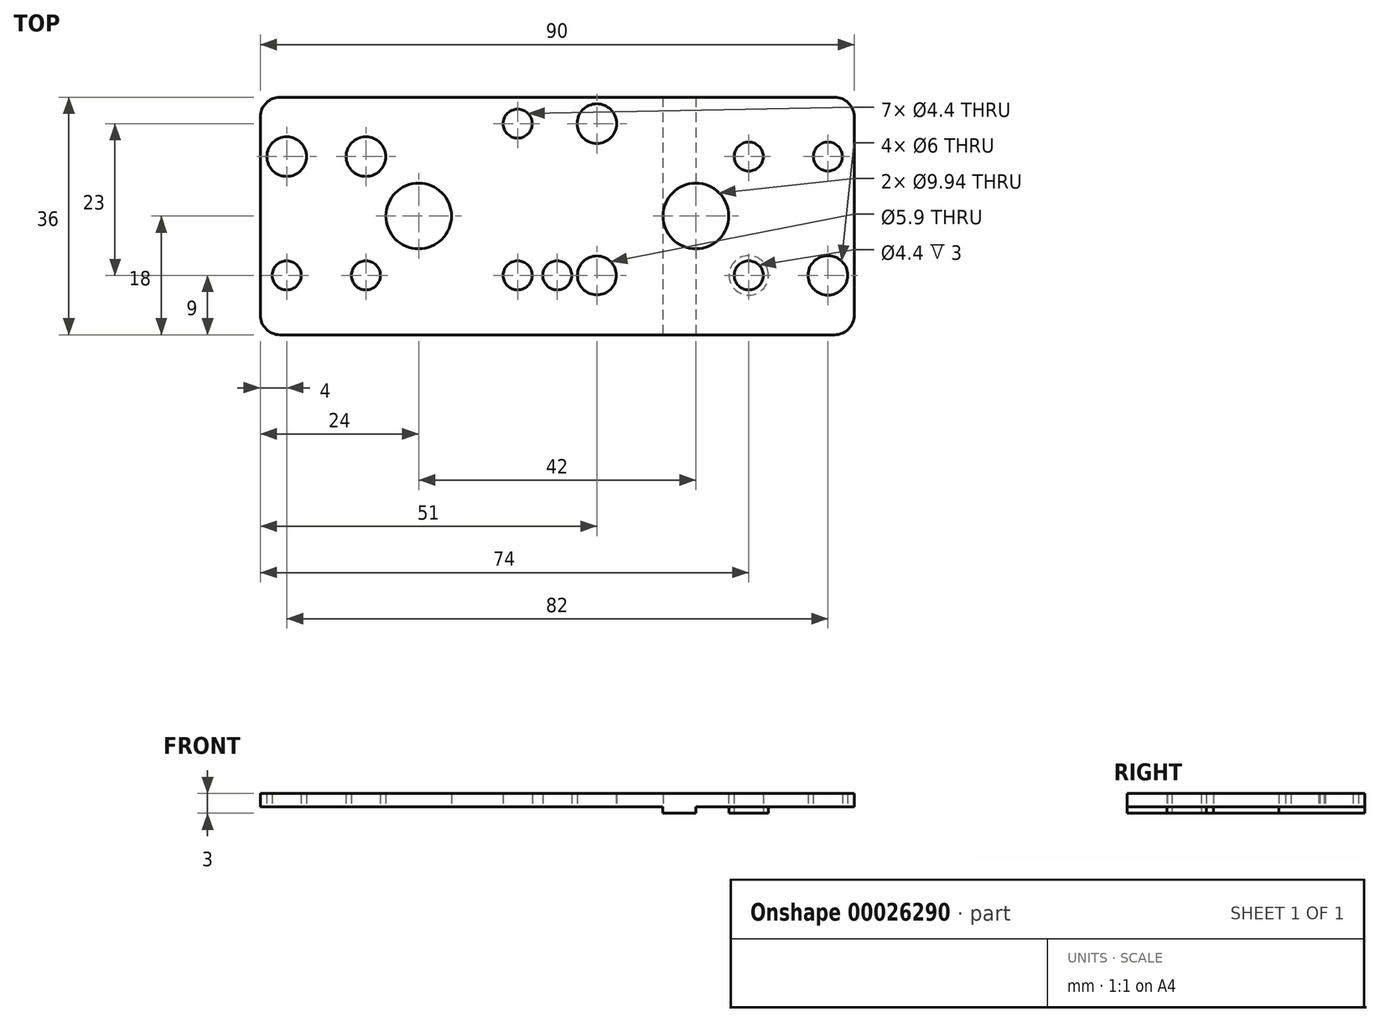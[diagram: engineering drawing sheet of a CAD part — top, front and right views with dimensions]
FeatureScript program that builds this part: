
annotation { "Feature Type Name" : "Feature", "Feature Type Description" : "" }
export const myFeature = defineFeature(function(context is Context, id is Id, definition is map)
    precondition{}
    {
        {
            var Q0;
            Q0=qCreatedBy(makeId("Top.planeOp"),FACE);
            var sketch = newSketch(context, id + "F0", { "sketchPlane" : qUnion([Q0])});
            skPoint(sketch, "E0", {"position": v(45, 0) * mm});
            skLineSegment(sketch, "E1", {"start": v(0, 0) * mm, "end": v(42, 0) * mm, "construction": true});
            skLineSegment(sketch, "E2.MirrorCS", {"start": v(0, 0) * mm, "end": v(-42, 0) * mm, "construction": true});
            skPoint(sketch, "E3", {"position": v(45, 36) * mm});
            skLineSegment(sketch, "E4", {"start": v(45, 3) * mm, "end": v(45, 33) * mm, "construction": true});
            skLineSegment(sketch, "E5", {"start": v(42, 36) * mm, "end": v(0, 36) * mm, "construction": true});
            skLineSegment(sketch, "E6", {"start": v(0, 36) * mm, "end": v(-42, 36) * mm, "construction": true});
            skLineSegment(sketch, "E7", {"start": v(-45, 3) * mm, "end": v(-45, 33) * mm, "construction": true});
            skPoint(sketch, "E8", {"position": v(-21, 36) * mm});
            skPoint(sketch, "E9", {"position": v(-16, 36) * mm});
            skLineSegment(sketch, "E10", {"start": v(-21, 36) * mm, "end": v(-21, 0) * mm, "construction": true});
            skLineSegment(sketch, "E11", {"start": v(-16, 36) * mm, "end": v(-16, 0) * mm, "construction": true});
            skLineSegment(sketch, "E12.MirrorCS", {"start": v(16, 36) * mm, "end": v(16, 0) * mm});
            skLineSegment(sketch, "E13.MirrorCS", {"start": v(21, 36) * mm, "end": v(21, 0) * mm});
            skPoint(sketch, "E14", {"position": v(-45, 9) * mm});
            skLineSegment(sketch, "E15", {"start": v(-45, 9) * mm, "end": v(45, 9) * mm, "construction": true});
            skCircle(sketch, "E16", {"center": v(-41, 9) * mm, "radius": 3 * mm});
            skCircle(sketch, "E17", {"center": v(-29, 9) * mm, "radius": 3 * mm});
            skCircle(sketch, "E18", {"center": v(-6, 9) * mm, "radius": 2.95 * mm});
            skCircle(sketch, "E19.MirrorC", {"center": v(6, 9) * mm, "radius": 2.95 * mm});
            skCircle(sketch, "E20.MirrorC", {"center": v(29, 9) * mm, "radius": 3 * mm});
            skCircle(sketch, "E21.MirrorC", {"center": v(41, 9) * mm, "radius": 3 * mm});
            skPoint(sketch, "E22", {"position": v(-45, 18) * mm});
            skLineSegment(sketch, "E23", {"start": v(-45, 18) * mm, "end": v(45, 18) * mm, "construction": true});
            skCircle(sketch, "E24.MirrorC", {"center": v(-41, 27) * mm, "radius": 3 * mm});
            skCircle(sketch, "E25.MirrorC", {"center": v(-29, 27) * mm, "radius": 3 * mm});
            skCircle(sketch, "E26.MirrorC", {"center": v(29, 27) * mm, "radius": 3 * mm});
            skCircle(sketch, "E27.MirrorC", {"center": v(41, 27) * mm, "radius": 3 * mm});
            skLineSegment(sketch, "E28", {"start": v(-45, 33) * mm, "end": v(-45, 3) * mm});
            skLineSegment(sketch, "E29", {"start": v(-42, 0) * mm, "end": v(42, 0) * mm});
            skLineSegment(sketch, "E30", {"start": v(45, 3) * mm, "end": v(45, 33) * mm});
            skLineSegment(sketch, "E31", {"start": v(42, 36) * mm, "end": v(-42, 36) * mm});
            skLineSegment(sketch, "E32", {"start": v(-6, 9) * mm, "end": v(-6, 36) * mm, "construction": true});
            skCircle(sketch, "E33", {"center": v(-6, 32) * mm, "radius": 3 * mm});
            skCircle(sketch, "E34.MirrorC", {"center": v(6, 32) * mm, "radius": 3 * mm});
            skPoint(sketch, "E35", {"position": v(21, 31.82) * mm});
            skPoint(sketch, "E36", {"position": v(0, 18) * mm});
            skCircle(sketch, "E37", {"center": v(0, 9) * mm, "radius": 2.95 * mm});
            skCircle(sketch, "E38", {"center": v(-6, 9) * mm, "radius": 2.2 * mm});
            skCircle(sketch, "E39", {"center": v(0, 9) * mm, "radius": 2.2 * mm});
            skCircle(sketch, "E40", {"center": v(6, 9) * mm, "radius": 2.2 * mm});
            skCircle(sketch, "E41", {"center": v(29, 27) * mm, "radius": 2.2 * mm});
            skCircle(sketch, "E42", {"center": v(41, 27) * mm, "radius": 2.2 * mm});
            skCircle(sketch, "E43", {"center": v(41, 9) * mm, "radius": 2.2 * mm});
            skCircle(sketch, "E44", {"center": v(29, 9) * mm, "radius": 2.2 * mm});
            skCircle(sketch, "E45", {"center": v(6, 32) * mm, "radius": 2.2 * mm});
            skCircle(sketch, "E46", {"center": v(-6, 32) * mm, "radius": 2.2 * mm});
            skCircle(sketch, "E47", {"center": v(-29, 27) * mm, "radius": 2.2 * mm});
            skCircle(sketch, "E48", {"center": v(-29, 9) * mm, "radius": 2.2 * mm});
            skCircle(sketch, "E49", {"center": v(-41, 27) * mm, "radius": 2.2 * mm});
            skCircle(sketch, "E50", {"center": v(-41, 9) * mm, "radius": 2.2 * mm});
            skPoint(sketch, "E51.visualSharp", {"position": v(-45, 36) * mm});
            skArc(sketch, "E51.filletArc", {"start": v(-42, 36) * mm, "mid": v(-44.12, 35.12) * mm, "end": v(-45, 33) * mm});
            skArc(sketch, "E52.MirrorCS", {"start": v(42, 36) * mm, "mid": v(44.12, 35.12) * mm, "end": v(45, 33) * mm});
            skArc(sketch, "E53.MirrorCS", {"start": v(42, 0) * mm, "mid": v(44.12, 0.88) * mm, "end": v(45, 3) * mm});
            skArc(sketch, "E54.MirrorCS", {"start": v(-42, 0) * mm, "mid": v(-44.12, 0.88) * mm, "end": v(-45, 3) * mm});
            skPoint(sketch, "E55.orphan", {"position": v(-45, 0) * mm});
            skLineSegment(sketch, "E56", {"start": v(-26.04, 27.5) * mm, "end": v(-26.04, 9.5) * mm, "construction": true});
            skCircle(sketch, "E57", {"center": v(-21, 18) * mm, "radius": 4.97 * mm});
            skCircle(sketch, "E58.MirrorC", {"center": v(21, 18) * mm, "radius": 4.97 * mm});
            skSolve(sketch);
        }
        {
            var Q0;
            {var subQ2=sQuery(id+"F0.wireOp",EDGE,"E12.MirrorCS");Q0=makeQuery(id+"F0.imprint","IMPRINT",FACE,{"disambiguationData":[TD([[makeQuery(id+"F0.imprint","IMPRINT",EDGE,{"derivedFrom":subQ2}),-1.0]])]});}
            var Q1;
            {var subQ2=sQuery(id+"F0.wireOp",EDGE,"E12.MirrorCS");Q1=makeQuery(id+"F0.imprint","IMPRINT",FACE,{"disambiguationData":[TD([[makeQuery(id+"F0.imprint","IMPRINT",EDGE,{"derivedFrom":subQ2}),1.0]])]});}
            var Q2;
            Q2=makeQuery(id+"F0.imprint","IMPRINT",FACE,{"disambiguationData":[TD([[makeQuery(id+"F0.imprint","IMPRINT",EDGE,{"derivedFrom":sQuery(id+"F0.wireOp",EDGE,"E33")}),1.0]])]});
            var Q3;
            Q3=makeQuery(id+"F0.imprint","IMPRINT",FACE,{"disambiguationData":[TD([[makeQuery(id+"F0.imprint","IMPRINT",EDGE,{"derivedFrom":sQuery(id+"F0.wireOp",EDGE,"E25.MirrorC")}),-1.0]])]});
            var Q4;
            Q4=makeQuery(id+"F0.imprint","IMPRINT",FACE,{"disambiguationData":[TD([[makeQuery(id+"F0.imprint","IMPRINT",EDGE,{"derivedFrom":sQuery(id+"F0.wireOp",EDGE,"E24.MirrorC")}),-1.0]])]});
            var Q5;
            Q5=makeQuery(id+"F0.imprint","IMPRINT",FACE,{"disambiguationData":[TD([[makeQuery(id+"F0.imprint","IMPRINT",EDGE,{"derivedFrom":sQuery(id+"F0.wireOp",EDGE,"E16")}),1.0]])]});
            var Q6;
            Q6=makeQuery(id+"F0.imprint","IMPRINT",FACE,{"disambiguationData":[TD([[makeQuery(id+"F0.imprint","IMPRINT",EDGE,{"derivedFrom":sQuery(id+"F0.wireOp",EDGE,"E18")}),1.0]])]});
            var Q7;
            Q7=makeQuery(id+"F0.imprint","IMPRINT",FACE,{"disambiguationData":[TD([[makeQuery(id+"F0.imprint","IMPRINT",EDGE,{"derivedFrom":sQuery(id+"F0.wireOp",EDGE,"E37")}),1.0]])]});
            var Q8;
            Q8=makeQuery(id+"F0.imprint","IMPRINT",FACE,{"disambiguationData":[TD([[makeQuery(id+"F0.imprint","IMPRINT",EDGE,{"derivedFrom":sQuery(id+"F0.wireOp",EDGE,"E19.MirrorC")}),-1.0]])]});
            var Q9;
            Q9=makeQuery(id+"F0.imprint","IMPRINT",FACE,{"disambiguationData":[TD([[makeQuery(id+"F0.imprint","IMPRINT",EDGE,{"derivedFrom":sQuery(id+"F0.wireOp",EDGE,"E34.MirrorC")}),-1.0]])]});
            var Q10;
            Q10=makeQuery(id+"F0.imprint","IMPRINT",FACE,{"disambiguationData":[TD([[makeQuery(id+"F0.imprint","IMPRINT",EDGE,{"derivedFrom":sQuery(id+"F0.wireOp",EDGE,"E26.MirrorC")}),1.0]])]});
            var Q11;
            Q11=makeQuery(id+"F0.imprint","IMPRINT",FACE,{"disambiguationData":[TD([[makeQuery(id+"F0.imprint","IMPRINT",EDGE,{"derivedFrom":sQuery(id+"F0.wireOp",EDGE,"E27.MirrorC")}),1.0]])]});
            var Q12;
            Q12=makeQuery(id+"F0.imprint","IMPRINT",FACE,{"disambiguationData":[TD([[makeQuery(id+"F0.imprint","IMPRINT",EDGE,{"derivedFrom":sQuery(id+"F0.wireOp",EDGE,"E20.MirrorC")}),-1.0]])]});
            var Q13;
            Q13=makeQuery(id+"F0.imprint","IMPRINT",FACE,{"disambiguationData":[TD([[makeQuery(id+"F0.imprint","IMPRINT",EDGE,{"derivedFrom":sQuery(id+"F0.wireOp",EDGE,"E21.MirrorC")}),-1.0]])]});
            var Q14;
            Q14=makeQuery(id+"F0.imprint","IMPRINT",FACE,{"disambiguationData":[TD([[makeQuery(id+"F0.imprint","IMPRINT",EDGE,{"derivedFrom":sQuery(id+"F0.wireOp",EDGE,"E17")}),1.0]])]});
            var Q15;
            Q15=makeQuery(id+"F0.imprint","IMPRINT",FACE,{"disambiguationData":[TD([[makeQuery(id+"F0.imprint","IMPRINT",EDGE,{"derivedFrom":sQuery(id+"F0.wireOp",EDGE,"E20.MirrorC")}),1.0]])]});
            extrude(context, id + "F1", {"entities" : qUnion([Q0, Q1, Q2, Q3, Q4, Q5, Q6, Q7, Q8, Q9, Q10, Q11, Q12, Q13, Q14, Q15]), "depth" : 3 * mm});
        }
        {
            var Q0;
            Q0=makeQuery(id+"F0.imprint","IMPRINT",FACE,{"disambiguationData":[TD([[makeQuery(id+"F0.imprint","IMPRINT",EDGE,{"derivedFrom":sQuery(id+"F0.wireOp",EDGE,"E24.MirrorC")}),-1.0]])]});
            var Q1;
            Q1=makeQuery(id+"F0.imprint","IMPRINT",FACE,{"disambiguationData":[TD([[makeQuery(id+"F0.imprint","IMPRINT",EDGE,{"derivedFrom":sQuery(id+"F0.wireOp",EDGE,"E16")}),1.0]])]});
            var Q2;
            Q2=makeQuery(id+"F0.imprint","IMPRINT",FACE,{"disambiguationData":[TD([[makeQuery(id+"F0.imprint","IMPRINT",EDGE,{"derivedFrom":sQuery(id+"F0.wireOp",EDGE,"E25.MirrorC")}),-1.0]])]});
            var Q3;
            Q3=makeQuery(id+"F0.imprint","IMPRINT",FACE,{"disambiguationData":[TD([[makeQuery(id+"F0.imprint","IMPRINT",EDGE,{"derivedFrom":sQuery(id+"F0.wireOp",EDGE,"E34.MirrorC")}),-1.0]])]});
            var Q4;
            Q4=makeQuery(id+"F0.imprint","IMPRINT",FACE,{"disambiguationData":[TD([[makeQuery(id+"F0.imprint","IMPRINT",EDGE,{"derivedFrom":sQuery(id+"F0.wireOp",EDGE,"E33")}),1.0]])]});
            var Q5;
            Q5=makeQuery(id+"F0.imprint","IMPRINT",FACE,{"disambiguationData":[TD([[makeQuery(id+"F0.imprint","IMPRINT",EDGE,{"derivedFrom":sQuery(id+"F0.wireOp",EDGE,"E18")}),1.0]])]});
            var Q6;
            Q6=makeQuery(id+"F0.imprint","IMPRINT",FACE,{"disambiguationData":[TD([[makeQuery(id+"F0.imprint","IMPRINT",EDGE,{"derivedFrom":sQuery(id+"F0.wireOp",EDGE,"E37")}),1.0]])]});
            var Q7;
            Q7=makeQuery(id+"F0.imprint","IMPRINT",FACE,{"disambiguationData":[TD([[makeQuery(id+"F0.imprint","IMPRINT",EDGE,{"derivedFrom":sQuery(id+"F0.wireOp",EDGE,"E19.MirrorC")}),-1.0]])]});
            var Q8;
            Q8=makeQuery(id+"F0.imprint","IMPRINT",FACE,{"disambiguationData":[TD([[makeQuery(id+"F0.imprint","IMPRINT",EDGE,{"derivedFrom":sQuery(id+"F0.wireOp",EDGE,"E20.MirrorC")}),-1.0]])]});
            var Q9;
            Q9=makeQuery(id+"F0.imprint","IMPRINT",FACE,{"disambiguationData":[TD([[makeQuery(id+"F0.imprint","IMPRINT",EDGE,{"derivedFrom":sQuery(id+"F0.wireOp",EDGE,"E21.MirrorC")}),-1.0]])]});
            var Q10;
            Q10=makeQuery(id+"F0.imprint","IMPRINT",FACE,{"disambiguationData":[TD([[makeQuery(id+"F0.imprint","IMPRINT",EDGE,{"derivedFrom":sQuery(id+"F0.wireOp",EDGE,"E27.MirrorC")}),1.0]])]});
            var Q11;
            Q11=makeQuery(id+"F0.imprint","IMPRINT",FACE,{"disambiguationData":[TD([[makeQuery(id+"F0.imprint","IMPRINT",EDGE,{"derivedFrom":sQuery(id+"F0.wireOp",EDGE,"E26.MirrorC")}),1.0]])]});
            var Q12;
            Q12=makeQuery(id+"F0.imprint","IMPRINT",FACE,{"disambiguationData":[TD([[makeQuery(id+"F0.imprint","IMPRINT",EDGE,{"derivedFrom":sQuery(id+"F0.wireOp",EDGE,"E17")}),1.0]])]});
            extrude(context, id + "F2", {"entities" : qUnion([Q0, Q1, Q2, Q3, Q4, Q5, Q6, Q7, Q8, Q9, Q10, Q11, Q12]), "operationType" : NewBodyOperationType.REMOVE, "depth" : 1 * mm});
        }
    });
